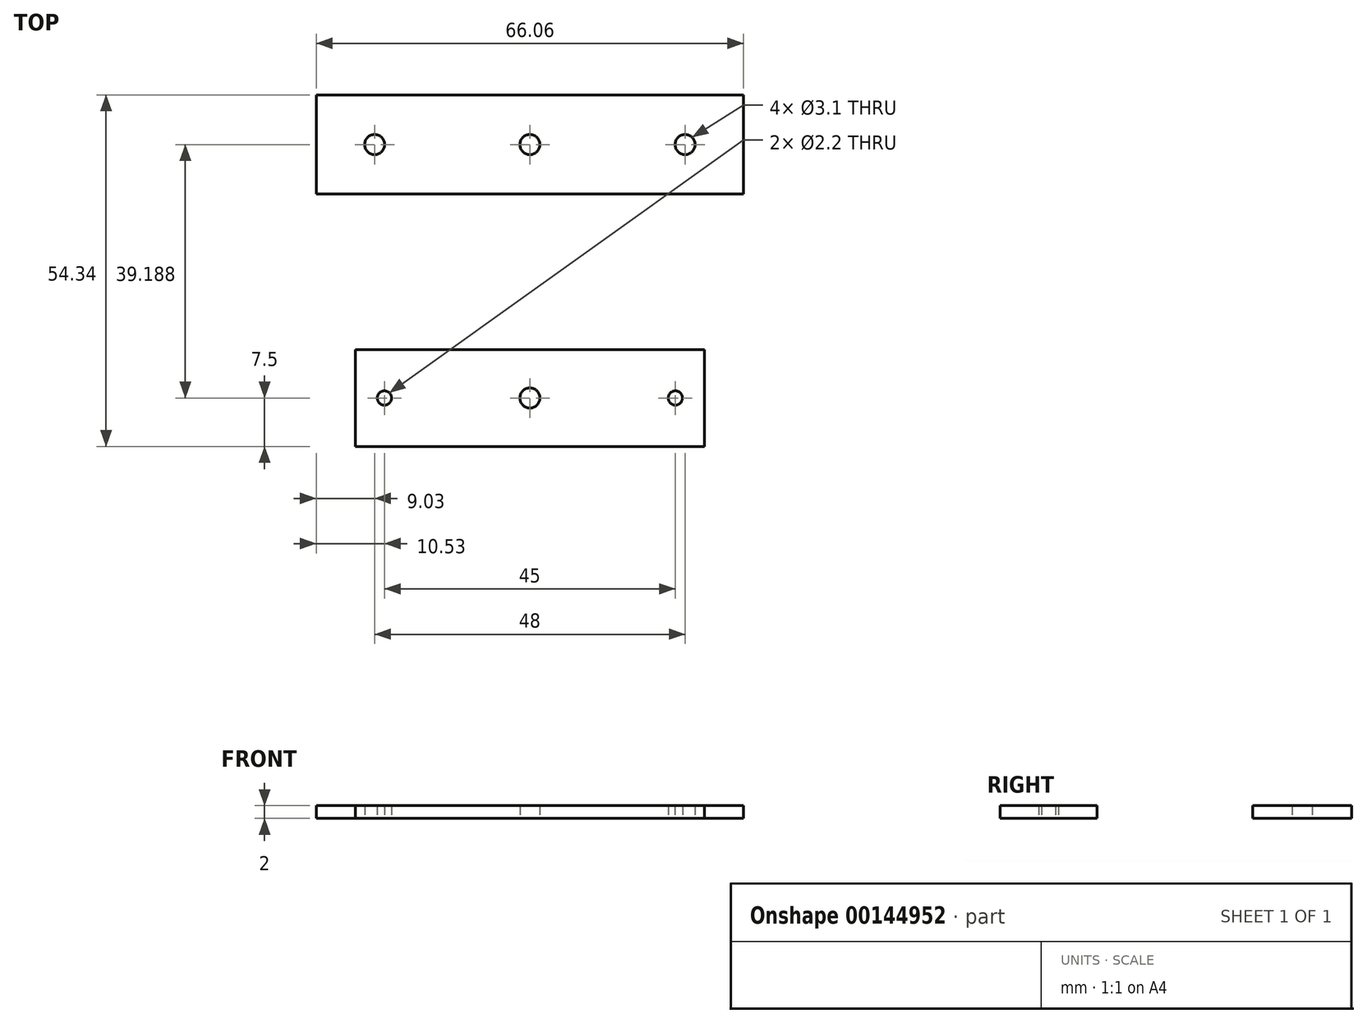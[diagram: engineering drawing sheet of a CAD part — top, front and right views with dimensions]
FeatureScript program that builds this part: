
annotation { "Feature Type Name" : "Feature", "Feature Type Description" : "" }
export const myFeature = defineFeature(function(context is Context, id is Id, definition is map)
    precondition{}
    {
        {
            var Q0;
            Q0=qCreatedBy(makeId("Top.planeOp"),FACE);
            var sketch = newSketch(context, id + "F0", { "sketchPlane" : qUnion([Q0])});
            skLineSegment(sketch, "E0.bottom", {"start": v(27, -7.5) * mm, "end": v(-27, -7.5) * mm});
            skLineSegment(sketch, "E0.top", {"start": v(27, 7.5) * mm, "end": v(-27, 7.5) * mm});
            skLineSegment(sketch, "E0.left", {"start": v(27, -7.5) * mm, "end": v(27, 7.5) * mm});
            skLineSegment(sketch, "E0.right", {"start": v(-27, -7.5) * mm, "end": v(-27, 7.5) * mm});
            skPoint(sketch, "E0.middle", {"position": v(0, 0) * mm});
            skCircle(sketch, "E1", {"center": v(-22.5, 0) * mm, "radius": 1.1 * mm});
            skCircle(sketch, "E2.MirrorC", {"center": v(22.5, 0) * mm, "radius": 1.1 * mm});
            skCircle(sketch, "E3", {"center": v(0, 0) * mm, "radius": 1.55 * mm});
            skLineSegment(sketch, "E4.bottom", {"start": v(33.03, 31.54) * mm, "end": v(-33.03, 31.54) * mm});
            skLineSegment(sketch, "E4.top", {"start": v(33.03, 46.84) * mm, "end": v(-33.03, 46.84) * mm});
            skLineSegment(sketch, "E4.left", {"start": v(33.03, 31.54) * mm, "end": v(33.03, 46.84) * mm});
            skLineSegment(sketch, "E4.right", {"start": v(-33.03, 31.54) * mm, "end": v(-33.03, 46.84) * mm});
            skPoint(sketch, "E4.middle", {"position": v(0, 39.19) * mm});
            skCircle(sketch, "E5", {"center": v(-24, 39.19) * mm, "radius": 1.55 * mm});
            skCircle(sketch, "E6.MirrorC", {"center": v(24, 39.19) * mm, "radius": 1.55 * mm});
            skCircle(sketch, "E7", {"center": v(0, 39.19) * mm, "radius": 1.55 * mm});
            skSolve(sketch);
        }
        {
            var Q0;
            Q0 = qSketchRegion(id + "F0", true);
            extrude(context, id + "F1", {"entities" : qUnion([Q0]), "depth" : 2 * mm});
        }
    });
